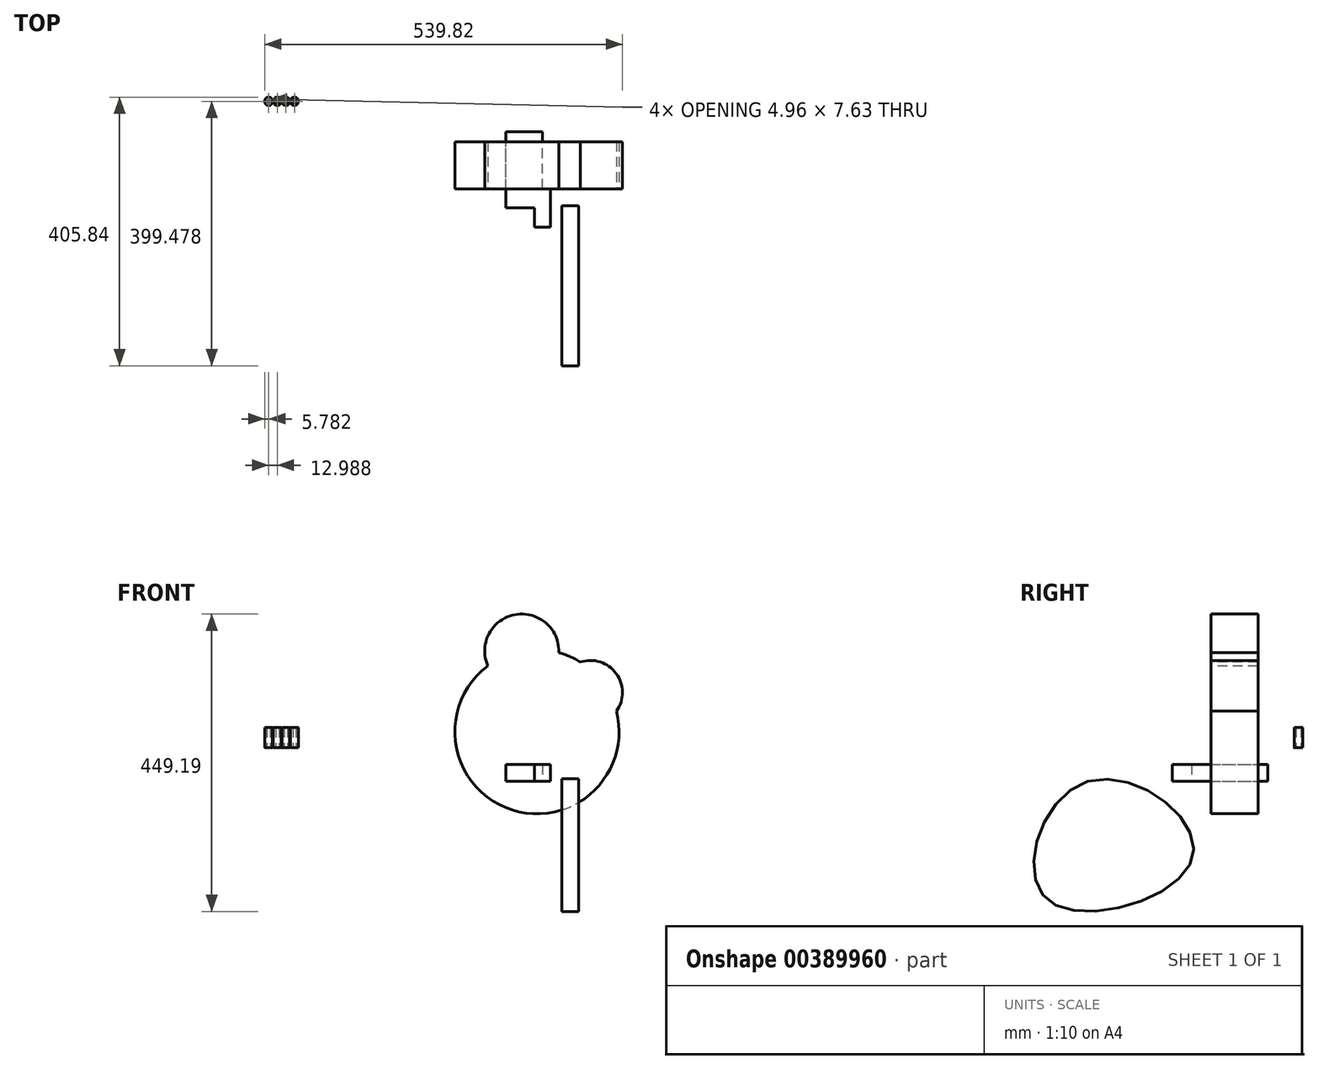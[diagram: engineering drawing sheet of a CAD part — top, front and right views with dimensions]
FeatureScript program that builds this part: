
annotation { "Feature Type Name" : "Feature", "Feature Type Description" : "" }
export const myFeature = defineFeature(function(context is Context, id is Id, definition is map)
    precondition{}
    {
        {
            var Q0;
            Q0=qCreatedBy(makeId("Top.planeOp"),FACE);
            var sketch = newSketch(context, id + "F0", { "sketchPlane" : qUnion([Q0])});
            skLineSegment(sketch, "E0.bottom", {"start": v(-41.35, 0) * mm, "end": v(-16.95, 0) * mm});
            skLineSegment(sketch, "E0.top", {"start": v(-41.35, -58.07) * mm, "end": v(-16.95, -58.07) * mm});
            skLineSegment(sketch, "E0.left", {"start": v(-41.35, 0) * mm, "end": v(-41.35, -58.07) * mm});
            skLineSegment(sketch, "E0.right", {"start": v(-16.95, 0) * mm, "end": v(-16.95, -58.07) * mm});
            skPoint(sketch, "E1.oppositeSnap0", {"position": v(-41.35, -29.03) * mm});
            skLineSegment(sketch, "E1.bottom", {"start": v(-41.35, -29.03) * mm, "end": v(-84.69, -29.03) * mm});
            skLineSegment(sketch, "E1.top", {"start": v(-41.35, -29.03) * mm, "end": v(-84.69, -29.03) * mm});
            skLineSegment(sketch, "E1.left", {"start": v(-41.35, -29.03) * mm, "end": v(-41.35, -29.03) * mm});
            skLineSegment(sketch, "E1.right", {"start": v(-84.69, -29.03) * mm, "end": v(-84.69, -29.03) * mm});
            skLineSegment(sketch, "E2.bottom", {"start": v(-84.69, -29.03) * mm, "end": v(-42.39, -29.03) * mm});
            skLineSegment(sketch, "E2.top", {"start": v(-84.69, 86.13) * mm, "end": v(-42.39, 86.13) * mm});
            skLineSegment(sketch, "E2.left", {"start": v(-84.69, -29.03) * mm, "end": v(-84.69, 86.13) * mm});
            skLineSegment(sketch, "E2.right", {"start": v(-42.39, -29.03) * mm, "end": v(-42.39, 86.13) * mm});
            skLineSegment(sketch, "E3.bottom", {"start": v(-29.15, 0) * mm, "end": v(-42.39, 0) * mm});
            skLineSegment(sketch, "E3.top", {"start": v(-29.15, 86.13) * mm, "end": v(-42.39, 86.13) * mm});
            skLineSegment(sketch, "E3.left", {"start": v(-29.15, 0) * mm, "end": v(-29.15, 86.13) * mm});
            skLineSegment(sketch, "E3.right", {"start": v(-42.39, 0) * mm, "end": v(-42.39, 86.13) * mm});
            skSolve(sketch);
        }
        {
            var Q0;
            Q0 = qSketchRegion(id + "F0", true);
            extrude(context, id + "F1", {"entities" : qUnion([Q0]), "depth" : 25.4 * mm});
        }
        {
            var Q0;
            Q0=qCreatedBy(makeId("Right.planeOp"),FACE);
            var sketch = newSketch(context, id + "F2", { "sketchPlane" : qUnion([Q0])});
            skFitSpline(sketch, "E4", {"points": [v(-185.47, 0) * mm, v(-27.32, -114.02) * mm, v(-247.46, -177.85) * mm, v(-185.47, 0) * mm]});
            skSolve(sketch);
        }
        {
            var Q0;
            Q0 = qSketchRegion(id + "F2", true);
            extrude(context, id + "F3", {"entities" : qUnion([Q0]), "depth" : 25.4 * mm});
        }
        {
            var Q0;
            Q0=qCreatedBy(makeId("Front.planeOp"),FACE);
            var sketch = newSketch(context, id + "F4", { "sketchPlane" : qUnion([Q0])});
            skText(sketch, "E5", { "text": "hello", "fontName": "Tinos-BoldItalic.ttf"});
            const initialGuessF4  = {"E5": [-0.30685, -0.18975, 1, 0, 0.34872]};
            skSetInitialGuess(sketch, initialGuessF4);
            skSolve(sketch);
        }
        {
            var Q0;
            Q0 = qConstructionFilter(qBodyType(qCreatedBy(id + "F4" ,EDGE), BodyType.WIRE), ConstructionObject.NO);
            extrude(context, id + "F5", {"bodyType" : ToolBodyType.SURFACE, "surfaceEntities" : qUnion([Q0]), "depth" : 25.4 * mm});
        }
        {
            var Q0;
            Q0=qCreatedBy(makeId("Front.planeOp"),FACE);
            var sketch = newSketch(context, id + "F6", { "sketchPlane" : qUnion([Q0])});
            skCircle(sketch, "E6", {"center": v(-37.58, 75.03) * mm, "radius": 123.96 * mm});
            skCircle(sketch, "E7", {"center": v(-60.46, 196.85) * mm, "radius": 55.96 * mm});
            skCircle(sketch, "E8", {"center": v(43.23, 134.46) * mm, "radius": 48.3 * mm});
            skSolve(sketch);
        }
        {
            var Q0;
            Q0 = qSketchRegion(id + "F6", true);
            extrude(context, id + "F7", {"entities" : qUnion([Q0]), "oppositeDirection" : true, "depth" : 71.12 * mm});
        }
        {
            var Q0;
            Q0=makeQuery(id+"F1.opExtrude","CAP_FACE",FACE,{"disambiguationData":[OSD([sQuery(id+"F0.wireOp",EDGE,"E0.bottom"),sQuery(id+"F0.wireOp",EDGE,"E0.top"),sQuery(id+"F0.wireOp",EDGE,"E0.left"),sQuery(id+"F0.wireOp",EDGE,"E0.right"),sQuery(id+"F0.wireOp",EDGE,"E1.top"),sQuery(id+"F0.wireOp",EDGE,"E2.bottom"),sQuery(id+"F0.wireOp",EDGE,"E2.top"),sQuery(id+"F0.wireOp",EDGE,"E2.left"),sQuery(id+"F0.wireOp",EDGE,"E3.top"),sQuery(id+"F0.wireOp",EDGE,"E3.left")])],"isStart":false});
            var sketch = newSketch(context, id + "F8", { "sketchPlane" : qUnion([Q0])});
            skText(sketch, "E9", { "text": "oooo", "fontName": "RobotoSlab-Bold.ttf"});
            const initialGuessF8  = {"E9": [-0.449, 0.12594, 1, 0, 0.01668]};
            skSetInitialGuess(sketch, initialGuessF8);
            skSolve(sketch);
        }
        {
            var Q0;
            Q0 = qSketchRegion(id + "F8", true);
            var Q1;
            Q1 = qConstructionFilter(qBodyType(qCreatedBy(id + "F8" ,EDGE), BodyType.WIRE), ConstructionObject.NO);
            extrude(context, id + "F9", {"entities" : qUnion([Q0]), "surfaceEntities" : qUnion([Q1]), "depth" : 55.88 * mm, "hasSecondDirection" : true, "secondDirectionOppositeDirection" : false, "secondDirectionDepth" : 25.4 * mm});
        }
    });
